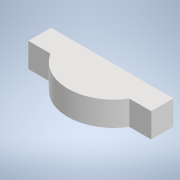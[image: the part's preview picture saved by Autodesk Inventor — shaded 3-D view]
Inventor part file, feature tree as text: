
AUTODESK INVENTOR PART (.ipt)
format: ipt  version: 2020 (Build 240168000, 168)  size: 138,240 bytes
history: native  units: mm
features: extrude x4, sketch x4
ambient origin geometry x8: Origin, YZ Plane, XZ Plane, XY Plane, X Axis, Y Axis, Z Axis, Center Point
bodies: Solido1 (feature_tree)
feature tree (8):
  extrude  "Estrusione1"  Depth=29.0mm
  extrude  "Estrusione2"  Depth=16.0mm TaperAngle=0.0deg
  extrude  "Estrusione3"  Depth=4.0mm TaperAngle=0.0deg
  extrude  "Estrusione4"  Depth=10.0mm TaperAngle=0.0deg
  sketch  "Schizzo1"
  sketch  "Schizzo2"
  sketch  "Schizzo3"
  sketch  "Schizzo5"
